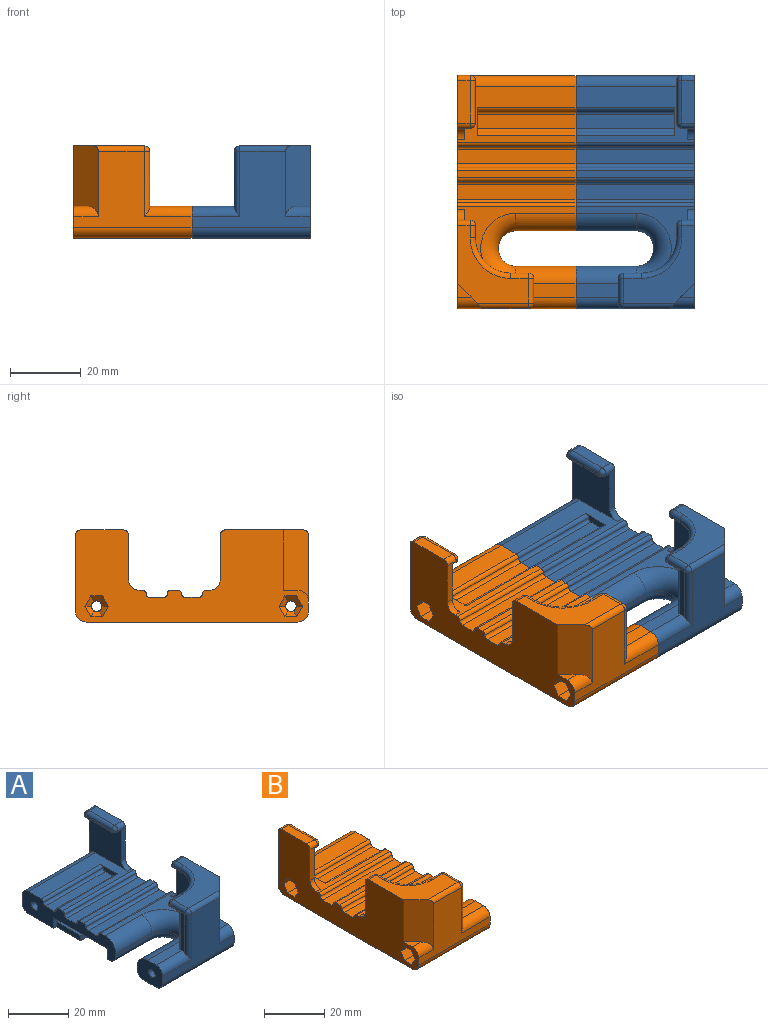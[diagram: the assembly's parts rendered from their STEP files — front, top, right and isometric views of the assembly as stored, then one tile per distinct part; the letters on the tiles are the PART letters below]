
ASSEMBLY  parts=2 mates=1
PART A: 111 faces, bbox 33.5x66x26.1 mm
  f0: plane 12x9mm, normal (-1,0,0), area 89.8mm2, adj f1,f3,f6,f33,f36,f62,f102,f105
  f1: plane 60x33.5mm, normal (0,0,-1), area 1501.4mm2, adj f0,f2,f8,f18,f20,f22,f23,f24
  f2: plane 44x9mm, normal (-1,0,0), area 236.8mm2, adj f1,f3,f4,f15,f16,f20,f21,f22
  f3: plane 33.5x26mm, normal (0,0,1), area 277.7mm2, adj f0,f2,f8,f11,f17,f27,f28,f29
  f4: plane 33.5x2mm, normal (0,0,1), area 67mm2, adj f2,f8,f97,f101
  f5: plane 22x20mm, normal (0,0,1), area 205.8mm2, adj f8,f66,f72,f74,f75,f76,f78,f80
  f6: plane 33.5x21.6mm, normal (0,-1,0), area 342.3mm2, adj f0,f8,f31,f33,f36,f66,f67,f80
  f7: plane 12x0.5mm, normal (-1,0,0), area 6mm2, adj f10,f32,f71,f83
  f8: plane 66x26.1mm, normal (1,0,0), area 1072.7mm2, adj f1,f3,f4,f5,f6,f14,f15,f16
  f9: plane 21.5x19.5mm, normal (0,0,-1), area 155.8mm2, adj f11,f13,f17,f25,f26,f27,f28,f29
  f10: plane 15x3mm, normal (0,0,-1), area 44mm2, adj f7,f12,f15,f32,f64,f71
  f11: plane 17x15.1mm, normal (-1,0,0), area 213.3mm2, adj f3,f9,f28,f63,f69
  f12: plane 18.1x18mm, normal (-1,0,0), area 230.4mm2, adj f10,f15,f16,f35,f64,f68
  f13: plane 5x0.5mm, normal (0,1,0), area 2.5mm2, adj f9,f25,f30,f76
  f14: plane 12x3.5mm, normal (0,0,1), area 42mm2, adj f8,f81,f83,f85
  f15: plane 33.5x21.6mm, normal (0,1,0), area 138.5mm2, adj f2,f8,f10,f12,f32,f34,f35,f85
  f16: plane 33.5x16mm, normal (0,0,1), area 282mm2, adj f2,f8,f12,f35,f68,f89,f91,f93
  f17: plane 15.1x12mm, normal (0,1,0), area 181.2mm2, adj f3,f9,f28,f29
  f18: plane 7.8x2.1mm, normal (0,-1,0), area 16.4mm2, adj f1,f19,f23,f24
  f19: plane 11.4x7.8mm, normal (0,0,1), area 88.9mm2, adj f18,f20,f23,f24
  f20: plane 9x4.2mm, normal (0,-1,0), area 21.4mm2, adj f1,f2,f19,f21,f23,f24
  f21: plane 25x9mm, normal (0,0,-1), area 225mm2, adj f2,f20,f22,f23
  f22: plane 9x4.2mm, normal (0,1,0), area 37.8mm2, adj f1,f2,f21,f23
  f23: plane 25x4.2mm, normal (-1,0,0), area 81.1mm2, adj f1,f18,f19,f20,f21,f22
  f24: plane 11.4x2.1mm, normal (-1,0,0), area 23.9mm2, adj f1,f18,f19,f20
  f25: cylinder r=10mm len=10mm, axis (0,0,1), area 7.9mm2, adj f9,f13,f26,f75
  f26: plane 3.5x0.5mm, normal (-1,0,0), area 1.8mm2, adj f9,f25,f70,f74
  f27: plane 16x7mm, normal (-1,0,0), area 33.9mm2, adj f3,f9,f29,f30,f31,f33,f78
  f28: cylinder r=6mm len=15.1mm, axis (0,0,1), area 142.3mm2, adj f3,f9,f11,f17
  f29: cylinder r=1.5mm len=15.1mm, axis (0,0,-1), area 35.6mm2, adj f3,f9,f17,f27
  f30: cylinder r=1.5mm len=1.5mm, axis (0,0,1), area 1.2mm2, adj f9,f13,f27,f77
  f31: cylinder r=1.5mm len=18.6mm, axis (0,0,1), area 40.4mm2, adj f6,f27,f33,f79
  f32: cylinder r=1.5mm len=1.5mm, axis (0,0,1), area 1.2mm2, adj f7,f10,f15,f84
  f33: cylinder r=3mm len=13.5mm, axis (-1,0,0), area 58.3mm2, adj f0,f3,f6,f27,f31
  f34: cylinder r=3mm len=33.5mm, axis (-1,0,0), area 157.9mm2, adj f1,f2,f8,f15
  f35: cylinder r=3mm len=31.5mm, axis (-1,0,0), area 148.4mm2, adj f2,f12,f15,f16
  f36: cylinder r=3mm len=33.5mm, axis (-1,0,0), area 157.9mm2, adj f0,f1,f6,f8
  f37: plane 28.3x3.35mm, normal (0,0,1), area 94.8mm2, adj f8,f38,f42,f54
  f38: plane 28.3x2.9mm, normal (0,0.87,0.5), area 94.8mm2, adj f8,f37,f39,f52
  f39: plane 28.3x2.9mm, normal (0,0.87,-0.5), area 94.8mm2, adj f8,f38,f40,f50
  f40: plane 28.3x3.35mm, normal (0,0,-1), area 94.8mm2, adj f8,f39,f41,f49
  f41: plane 28.3x2.9mm, normal (0,-0.87,-0.5), area 94.8mm2, adj f8,f40,f42,f51
  f42: plane 28.3x2.9mm, normal (0,-0.87,0.5), area 94.8mm2, adj f8,f37,f41,f53
  f43: plane 28.3x2.9mm, normal (0,-0.87,0.5), area 94.8mm2, adj f8,f44,f48,f59
  f44: plane 28.3x3.35mm, normal (0,0,1), area 94.8mm2, adj f8,f43,f45,f60
  f45: plane 28.3x2.9mm, normal (0,0.87,0.5), area 94.8mm2, adj f8,f44,f46,f58
  f46: plane 28.3x2.9mm, normal (0,0.87,-0.5), area 94.8mm2, adj f8,f45,f47,f56
  f47: plane 28.3x3.35mm, normal (0,0,-1), area 94.8mm2, adj f8,f46,f48,f55
  f48: plane 28.3x2.9mm, normal (0,-0.87,-0.5), area 94.8mm2, adj f8,f43,f47,f57
  f49: plane 3.35x1.6mm, normal (0.71,0,-0.71), area 5.2mm2, adj f40,f50,f51,f62
  f50: plane 2.9x2.6mm, normal (0.71,0.61,-0.35), area 5.2mm2, adj f39,f49,f52,f62
  f51: plane 2.9x2.6mm, normal (0.71,-0.61,-0.35), area 5.2mm2, adj f41,f49,f53,f62
  f52: plane 2.9x2.6mm, normal (0.71,0.61,0.35), area 5.2mm2, adj f38,f50,f54,f62
  f53: plane 2.9x2.6mm, normal (0.71,-0.61,0.35), area 5.2mm2, adj f42,f51,f54,f62
  f54: plane 3.35x1.6mm, normal (0.71,0,0.71), area 5.2mm2, adj f37,f52,f53,f62
  f55: plane 3.35x1.6mm, normal (0.71,0,-0.71), area 5.2mm2, adj f47,f56,f57,f61
  f56: plane 2.9x2.6mm, normal (0.71,0.61,-0.35), area 5.2mm2, adj f46,f55,f58,f61
  f57: plane 2.9x2.6mm, normal (0.71,-0.61,-0.35), area 5.2mm2, adj f48,f55,f59,f61
  f58: plane 2.9x2.6mm, normal (0.71,0.61,0.35), area 5.2mm2, adj f45,f56,f60,f61
  f59: plane 2.9x2.6mm, normal (0.71,-0.61,0.35), area 5.2mm2, adj f43,f57,f60,f61
  f60: plane 3.35x1.6mm, normal (0.71,0,0.71), area 5.2mm2, adj f44,f58,f59,f61
  f61: cylinder r=1.5mm len=3.8mm, axis (1,0,0), area 35.2mm2, adj f2,f55,f56,f57,f58,f59,f60
  f62: cylinder r=1.5mm len=3.8mm, axis (1,0,0), area 35.2mm2, adj f0,f49,f50,f51,f52,f53,f54
  f63: plane 12.6x3.5mm, normal (0,1,0), area 26mm2, adj f8,f9,f11,f69,f70,f72
  f64: plane 12.6x3.5mm, normal (0,-1,0), area 26mm2, adj f8,f10,f12,f68,f71,f81
  f65: plane 4x4mm, normal (0,0,1), area 8mm2, adj f8,f66,f67
  f66: plane 20.1x7mm, normal (0.71,-0.71,0), area 171.3mm2, adj f5,f6,f8,f65,f67,f80
  f67: cylinder r=3mm len=7mm, axis (-1,0,0), area 27.8mm2, adj f6,f8,f65,f66
  f68: cylinder r=3mm len=3mm, axis (-1,0,0), area 9.4mm2, adj f8,f12,f16,f64
  f69: cylinder r=3mm len=3mm, axis (1,0,0), area 9.4mm2, adj f3,f8,f11,f63
  f70: cylinder r=1.5mm len=1.5mm, axis (0,0,-1), area 1.2mm2, adj f9,f26,f63,f73
  f71: cylinder r=1.5mm len=1.5mm, axis (0,0,-1), area 1.2mm2, adj f7,f10,f64,f82
  f72: cylinder r=1.5mm len=3.5mm, axis (-1,0,0), area 8.2mm2, adj f5,f8,f63,f73
  f73: sphere r=1.5mm, area 3.5mm2, adj f70,f72,f74
  f74: cylinder r=1.5mm len=3.5mm, axis (0,-1,0), area 8.2mm2, adj f5,f26,f73,f75
  f75: torus R=11.5mm, axis (0,0,-1), area 39mm2, adj f5,f25,f74,f76
  f76: cylinder r=1.5mm len=5mm, axis (-1,0,0), area 11.8mm2, adj f5,f13,f75,f77
  f77: sphere r=1.5mm, area 3.5mm2, adj f30,f76,f78
  f78: cylinder r=1.5mm len=7mm, axis (0,-1,0), area 16.5mm2, adj f5,f27,f77,f79
  f79: sphere r=1.5mm, area 3.5mm2, adj f31,f78,f80
  f80: cylinder r=1.5mm len=14.5mm, axis (-1,0,0), area 31.9mm2, adj f5,f6,f66,f79
  f81: cylinder r=1.5mm len=3.5mm, axis (1,0,0), area 8.2mm2, adj f8,f14,f64,f82
  f82: sphere r=1.5mm, area 3.5mm2, adj f71,f81,f83
  f83: cylinder r=1.5mm len=12mm, axis (0,-1,0), area 28.3mm2, adj f7,f14,f82,f84
  f84: sphere r=1.5mm, area 3.5mm2, adj f32,f83,f85
  f85: cylinder r=1.5mm len=3.5mm, axis (-1,0,0), area 8.2mm2, adj f8,f14,f15,f84
  f86: plane 33.5x4mm, normal (0,0,1), area 134mm2, adj f2,f8,f95,f96
  f87: plane 33.5x4mm, normal (0,0,1), area 134mm2, adj f2,f8,f99,f100
  f88: plane 28x4mm, normal (0,0,1), area 112mm2, adj f2,f89,f90,f92
  f89: plane 8x2mm, normal (-1,0,0), area 12mm2, adj f16,f88,f90,f91,f92,f93
  f90: cylinder r=1mm len=28mm, axis (-1,0,0), area 44mm2, adj f2,f88,f89,f91
  f91: cylinder r=1mm len=28mm, axis (1,0,0), area 44mm2, adj f2,f16,f89,f90
  f92: cylinder r=1mm len=28mm, axis (1,0,0), area 44mm2, adj f2,f88,f89,f93
  f93: cylinder r=1mm len=28mm, axis (-1,0,0), area 44mm2, adj f2,f16,f89,f92
  f94: cylinder r=1mm len=33.5mm, axis (-1,0,0), area 52.6mm2, adj f2,f8,f16,f95
  f95: cylinder r=1mm len=33.5mm, axis (1,0,0), area 52.6mm2, adj f2,f8,f86,f94
  f96: cylinder r=1mm len=33.5mm, axis (1,0,0), area 52.6mm2, adj f2,f8,f86,f97
  f97: cylinder r=1mm len=33.5mm, axis (-1,0,0), area 52.6mm2, adj f2,f4,f8,f96
  f98: cylinder r=1mm len=33.5mm, axis (-1,0,0), area 52.6mm2, adj f2,f3,f8,f99
  f99: cylinder r=1mm len=33.5mm, axis (1,0,0), area 52.6mm2, adj f2,f8,f87,f98
  f100: cylinder r=1mm len=33.5mm, axis (1,0,0), area 52.6mm2, adj f2,f8,f87,f101
  f101: cylinder r=1mm len=33.5mm, axis (-1,0,0), area 52.6mm2, adj f2,f4,f8,f100
  f102: plane 17x1mm, normal (0,1,0), area 17mm2, adj f0,f104,f105,f110
  f103: plane 17x1mm, normal (0,-1,0), area 17mm2, adj f2,f104,f107,f108
  f104: cylinder r=5mm len=10mm, axis (0,0,1), area 15.7mm2, adj f102,f103,f106,f109
  f105: cylinder r=5mm len=17mm, axis (-1,0,0), area 133.5mm2, adj f0,f3,f102,f106
  f106: torus R=10mm, axis (0,0,-1), area 168.2mm2, adj f3,f104,f105,f107
  f107: cylinder r=5mm len=17mm, axis (1,0,0), area 133.5mm2, adj f2,f3,f103,f106
  f108: cylinder r=3mm len=17mm, axis (1,0,0), area 80.1mm2, adj f1,f2,f103,f109
  f109: torus R=8mm, axis (0,0,1), area 90.2mm2, adj f1,f104,f108,f110
  f110: cylinder r=3mm len=17mm, axis (-1,0,0), area 80.1mm2, adj f0,f1,f102,f109
PART B: 111 faces, bbox 33.5x66x26.1 mm
  f0: plane 12x9mm, normal (1,0,0), area 89.8mm2, adj f1,f3,f6,f33,f36,f62,f102,f105
  f1: plane 60x33.5mm, normal (0,0,-1), area 1501.4mm2, adj f0,f2,f8,f18,f20,f22,f23,f24
  f2: plane 44x9mm, normal (1,0,0), area 236.8mm2, adj f1,f3,f4,f15,f16,f20,f21,f22
  f3: plane 33.5x26mm, normal (0,0,1), area 277.7mm2, adj f0,f2,f8,f11,f17,f27,f28,f29
  f4: plane 33.5x2mm, normal (0,0,1), area 67mm2, adj f2,f8,f97,f101
  f5: plane 22x20mm, normal (0,0,1), area 205.8mm2, adj f8,f66,f72,f74,f75,f76,f78,f80
  f6: plane 33.5x21.6mm, normal (0,-1,0), area 342.3mm2, adj f0,f8,f31,f33,f36,f66,f67,f80
  f7: plane 12x0.5mm, normal (1,0,0), area 6mm2, adj f10,f32,f71,f83
  f8: plane 66x26.1mm, normal (-1,0,0), area 1072.7mm2, adj f1,f3,f4,f5,f6,f14,f15,f16
  f9: plane 21.5x19.5mm, normal (0,0,-1), area 155.8mm2, adj f11,f13,f17,f25,f26,f27,f28,f29
  f10: plane 15x3mm, normal (0,0,-1), area 44mm2, adj f7,f12,f15,f32,f64,f71
  f11: plane 17x15.1mm, normal (1,0,0), area 213.3mm2, adj f3,f9,f28,f63,f69
  f12: plane 18.1x18mm, normal (1,0,0), area 230.4mm2, adj f10,f15,f16,f35,f64,f68
  f13: plane 5x0.5mm, normal (0,1,0), area 2.5mm2, adj f9,f25,f30,f76
  f14: plane 12x3.5mm, normal (0,0,1), area 42mm2, adj f8,f81,f83,f85
  f15: plane 33.5x21.6mm, normal (0,1,0), area 138.5mm2, adj f2,f8,f10,f12,f32,f34,f35,f85
  f16: plane 33.5x16mm, normal (0,0,1), area 282mm2, adj f2,f8,f12,f35,f68,f89,f91,f93
  f17: plane 15.1x12mm, normal (0,1,0), area 181.2mm2, adj f3,f9,f28,f29
  f18: plane 7.8x2.1mm, normal (0,-1,0), area 16.4mm2, adj f1,f19,f23,f24
  f19: plane 11.4x7.8mm, normal (0,0,1), area 88.9mm2, adj f18,f20,f23,f24
  f20: plane 9x4.2mm, normal (0,-1,0), area 21.4mm2, adj f1,f2,f19,f21,f23,f24
  f21: plane 25x9mm, normal (0,0,-1), area 225mm2, adj f2,f20,f22,f23
  f22: plane 9x4.2mm, normal (0,1,0), area 37.8mm2, adj f1,f2,f21,f23
  f23: plane 25x4.2mm, normal (1,0,0), area 81.1mm2, adj f1,f18,f19,f20,f21,f22
  f24: plane 11.4x2.1mm, normal (1,0,0), area 23.9mm2, adj f1,f18,f19,f20
  f25: cylinder r=10mm len=10mm, axis (0,0,1), area 7.9mm2, adj f9,f13,f26,f75
  f26: plane 3.5x0.5mm, normal (1,0,0), area 1.8mm2, adj f9,f25,f70,f74
  f27: plane 16x7mm, normal (1,0,0), area 33.9mm2, adj f3,f9,f29,f30,f31,f33,f78
  f28: cylinder r=6mm len=15.1mm, axis (0,0,1), area 142.3mm2, adj f3,f9,f11,f17
  f29: cylinder r=1.5mm len=15.1mm, axis (0,0,-1), area 35.6mm2, adj f3,f9,f17,f27
  f30: cylinder r=1.5mm len=1.5mm, axis (0,0,1), area 1.2mm2, adj f9,f13,f27,f77
  f31: cylinder r=1.5mm len=18.6mm, axis (0,0,1), area 40.4mm2, adj f6,f27,f33,f79
  f32: cylinder r=1.5mm len=1.5mm, axis (0,0,1), area 1.2mm2, adj f7,f10,f15,f84
  f33: cylinder r=3mm len=13.5mm, axis (1,0,0), area 58.3mm2, adj f0,f3,f6,f27,f31
  f34: cylinder r=3mm len=33.5mm, axis (1,0,0), area 157.9mm2, adj f1,f2,f8,f15
  f35: cylinder r=3mm len=31.5mm, axis (1,0,0), area 148.4mm2, adj f2,f12,f15,f16
  f36: cylinder r=3mm len=33.5mm, axis (1,0,0), area 157.9mm2, adj f0,f1,f6,f8
  f37: plane 28.3x3.35mm, normal (0,0,1), area 94.8mm2, adj f8,f38,f42,f54
  f38: plane 28.3x2.9mm, normal (0,0.87,0.5), area 94.8mm2, adj f8,f37,f39,f52
  f39: plane 28.3x2.9mm, normal (0,0.87,-0.5), area 94.8mm2, adj f8,f38,f40,f50
  f40: plane 28.3x3.35mm, normal (0,0,-1), area 94.8mm2, adj f8,f39,f41,f49
  f41: plane 28.3x2.9mm, normal (0,-0.87,-0.5), area 94.8mm2, adj f8,f40,f42,f51
  f42: plane 28.3x2.9mm, normal (0,-0.87,0.5), area 94.8mm2, adj f8,f37,f41,f53
  f43: plane 28.3x2.9mm, normal (0,-0.87,0.5), area 94.8mm2, adj f8,f44,f48,f59
  f44: plane 28.3x3.35mm, normal (0,0,1), area 94.8mm2, adj f8,f43,f45,f60
  f45: plane 28.3x2.9mm, normal (0,0.87,0.5), area 94.8mm2, adj f8,f44,f46,f58
  f46: plane 28.3x2.9mm, normal (0,0.87,-0.5), area 94.8mm2, adj f8,f45,f47,f56
  f47: plane 28.3x3.35mm, normal (0,0,-1), area 94.8mm2, adj f8,f46,f48,f55
  f48: plane 28.3x2.9mm, normal (0,-0.87,-0.5), area 94.8mm2, adj f8,f43,f47,f57
  f49: plane 3.35x1.6mm, normal (-0.71,0,-0.71), area 5.2mm2, adj f40,f50,f51,f62
  f50: plane 2.9x2.6mm, normal (-0.71,0.61,-0.35), area 5.2mm2, adj f39,f49,f52,f62
  f51: plane 2.9x2.6mm, normal (-0.71,-0.61,-0.35), area 5.2mm2, adj f41,f49,f53,f62
  f52: plane 2.9x2.6mm, normal (-0.71,0.61,0.35), area 5.2mm2, adj f38,f50,f54,f62
  f53: plane 2.9x2.6mm, normal (-0.71,-0.61,0.35), area 5.2mm2, adj f42,f51,f54,f62
  f54: plane 3.35x1.6mm, normal (-0.71,0,0.71), area 5.2mm2, adj f37,f52,f53,f62
  f55: plane 3.35x1.6mm, normal (-0.71,0,-0.71), area 5.2mm2, adj f47,f56,f57,f61
  f56: plane 2.9x2.6mm, normal (-0.71,0.61,-0.35), area 5.2mm2, adj f46,f55,f58,f61
  f57: plane 2.9x2.6mm, normal (-0.71,-0.61,-0.35), area 5.2mm2, adj f48,f55,f59,f61
  f58: plane 2.9x2.6mm, normal (-0.71,0.61,0.35), area 5.2mm2, adj f45,f56,f60,f61
  f59: plane 2.9x2.6mm, normal (-0.71,-0.61,0.35), area 5.2mm2, adj f43,f57,f60,f61
  f60: plane 3.35x1.6mm, normal (-0.71,0,0.71), area 5.2mm2, adj f44,f58,f59,f61
  f61: cylinder r=1.5mm len=3.8mm, axis (-1,0,0), area 35.2mm2, adj f2,f55,f56,f57,f58,f59,f60
  f62: cylinder r=1.5mm len=3.8mm, axis (-1,0,0), area 35.2mm2, adj f0,f49,f50,f51,f52,f53,f54
  f63: plane 12.6x3.5mm, normal (0,1,0), area 26mm2, adj f8,f9,f11,f69,f70,f72
  f64: plane 12.6x3.5mm, normal (0,-1,0), area 26mm2, adj f8,f10,f12,f68,f71,f81
  f65: plane 4x4mm, normal (0,0,1), area 8mm2, adj f8,f66,f67
  f66: plane 20.1x7mm, normal (-0.71,-0.71,0), area 171.3mm2, adj f5,f6,f8,f65,f67,f80
  f67: cylinder r=3mm len=7mm, axis (1,0,0), area 27.8mm2, adj f6,f8,f65,f66
  f68: cylinder r=3mm len=3mm, axis (1,0,0), area 9.4mm2, adj f8,f12,f16,f64
  f69: cylinder r=3mm len=3mm, axis (-1,0,0), area 9.4mm2, adj f3,f8,f11,f63
  f70: cylinder r=1.5mm len=1.5mm, axis (0,0,-1), area 1.2mm2, adj f9,f26,f63,f73
  f71: cylinder r=1.5mm len=1.5mm, axis (0,0,-1), area 1.2mm2, adj f7,f10,f64,f82
  f72: cylinder r=1.5mm len=3.5mm, axis (1,0,0), area 8.2mm2, adj f5,f8,f63,f73
  f73: sphere r=1.5mm, area 3.5mm2, adj f70,f72,f74
  f74: cylinder r=1.5mm len=3.5mm, axis (0,-1,0), area 8.2mm2, adj f5,f26,f73,f75
  f75: torus R=11.5mm, axis (0,0,-1), area 39mm2, adj f5,f25,f74,f76
  f76: cylinder r=1.5mm len=5mm, axis (1,0,0), area 11.8mm2, adj f5,f13,f75,f77
  f77: sphere r=1.5mm, area 3.5mm2, adj f30,f76,f78
  f78: cylinder r=1.5mm len=7mm, axis (0,-1,0), area 16.5mm2, adj f5,f27,f77,f79
  f79: sphere r=1.5mm, area 3.5mm2, adj f31,f78,f80
  f80: cylinder r=1.5mm len=14.5mm, axis (1,0,0), area 31.9mm2, adj f5,f6,f66,f79
  f81: cylinder r=1.5mm len=3.5mm, axis (-1,0,0), area 8.2mm2, adj f8,f14,f64,f82
  f82: sphere r=1.5mm, area 3.5mm2, adj f71,f81,f83
  f83: cylinder r=1.5mm len=12mm, axis (0,-1,0), area 28.3mm2, adj f7,f14,f82,f84
  f84: sphere r=1.5mm, area 3.5mm2, adj f32,f83,f85
  f85: cylinder r=1.5mm len=3.5mm, axis (1,0,0), area 8.2mm2, adj f8,f14,f15,f84
  f86: plane 33.5x4mm, normal (0,0,1), area 134mm2, adj f2,f8,f95,f96
  f87: plane 33.5x4mm, normal (0,0,1), area 134mm2, adj f2,f8,f99,f100
  f88: plane 28x4mm, normal (0,0,1), area 112mm2, adj f2,f89,f90,f92
  f89: plane 8x2mm, normal (1,0,0), area 12mm2, adj f16,f88,f90,f91,f92,f93
  f90: cylinder r=1mm len=28mm, axis (1,0,0), area 44mm2, adj f2,f88,f89,f91
  f91: cylinder r=1mm len=28mm, axis (-1,0,0), area 44mm2, adj f2,f16,f89,f90
  f92: cylinder r=1mm len=28mm, axis (-1,0,0), area 44mm2, adj f2,f88,f89,f93
  f93: cylinder r=1mm len=28mm, axis (1,0,0), area 44mm2, adj f2,f16,f89,f92
  f94: cylinder r=1mm len=33.5mm, axis (1,0,0), area 52.6mm2, adj f2,f8,f16,f95
  f95: cylinder r=1mm len=33.5mm, axis (-1,0,0), area 52.6mm2, adj f2,f8,f86,f94
  f96: cylinder r=1mm len=33.5mm, axis (-1,0,0), area 52.6mm2, adj f2,f8,f86,f97
  f97: cylinder r=1mm len=33.5mm, axis (1,0,0), area 52.6mm2, adj f2,f4,f8,f96
  f98: cylinder r=1mm len=33.5mm, axis (1,0,0), area 52.6mm2, adj f2,f3,f8,f99
  f99: cylinder r=1mm len=33.5mm, axis (-1,0,0), area 52.6mm2, adj f2,f8,f87,f98
  f100: cylinder r=1mm len=33.5mm, axis (-1,0,0), area 52.6mm2, adj f2,f8,f87,f101
  f101: cylinder r=1mm len=33.5mm, axis (1,0,0), area 52.6mm2, adj f2,f4,f8,f100
  f102: plane 17x1mm, normal (0,1,0), area 17mm2, adj f0,f104,f105,f110
  f103: plane 17x1mm, normal (0,-1,0), area 17mm2, adj f2,f104,f107,f108
  f104: cylinder r=5mm len=10mm, axis (0,0,1), area 15.7mm2, adj f102,f103,f106,f109
  f105: cylinder r=5mm len=17mm, axis (1,0,0), area 133.5mm2, adj f0,f3,f102,f106
  f106: torus R=10mm, axis (0,0,-1), area 168.2mm2, adj f3,f104,f105,f107
  f107: cylinder r=5mm len=17mm, axis (-1,0,0), area 133.5mm2, adj f2,f3,f103,f106
  f108: cylinder r=3mm len=17mm, axis (-1,0,0), area 80.1mm2, adj f1,f2,f103,f109
  f109: torus R=8mm, axis (0,0,1), area 90.2mm2, adj f1,f104,f108,f110
  f110: cylinder r=3mm len=17mm, axis (1,0,0), area 80.1mm2, adj f0,f1,f102,f109
PLACE A at identity
PLACE B at identity fixed
MATE fastened B.f62 <-> A.f62  axis (1,0,0) through (0,5,4.5)mm
